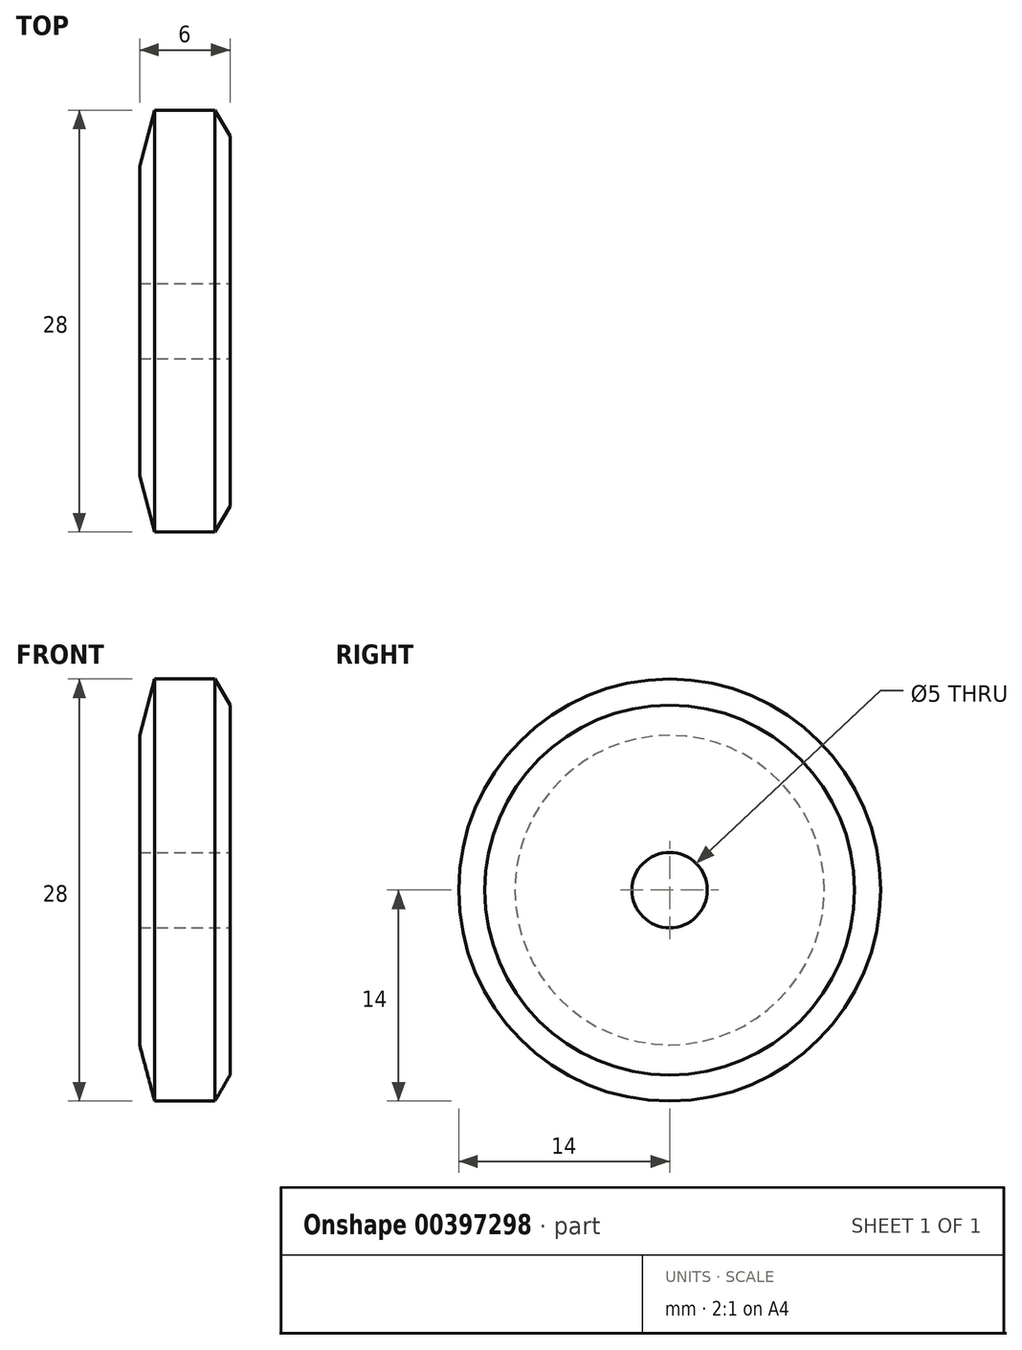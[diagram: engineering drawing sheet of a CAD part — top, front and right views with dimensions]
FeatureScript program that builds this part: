
annotation { "Feature Type Name" : "Feature", "Feature Type Description" : "" }
export const myFeature = defineFeature(function(context is Context, id is Id, definition is map)
    precondition{}
    {
        {
            var Q0;
            Q0=qCreatedBy(makeId("Front.planeOp"),FACE);
            var sketch = newSketch(context, id + "F0", { "sketchPlane" : qUnion([Q0])});
            skLineSegment(sketch, "E0", {"start": v(0, 0) * mm, "end": v(0, 14) * mm});
            skLineSegment(sketch, "E1", {"start": v(0, 14) * mm, "end": v(6, 14) * mm});
            skLineSegment(sketch, "E2", {"start": v(6, 14) * mm, "end": v(6, 0) * mm});
            skLineSegment(sketch, "E3", {"start": v(6, 0) * mm, "end": v(0, 0) * mm});
            skLineSegment(sketch, "E4", {"start": v(0, 3) * mm, "end": v(6, 3) * mm, "construction": true});
            skLineSegment(sketch, "E5", {"start": v(1, 14) * mm, "end": v(0, 10.27) * mm});
            skLineSegment(sketch, "E6", {"start": v(5, 14) * mm, "end": v(6, 12.27) * mm});
            skSolve(sketch);
        }
        {
            var Q0;
            {var subQ0=sQuery(id+"F0.wireOp",EDGE,"E3");Q0=makeQuery(id+"F0.imprint","IMPRINT",FACE,{"disambiguationData":[TD([[makeQuery(id+"F0.imprint","IMPRINT",EDGE,{"derivedFrom":subQ0}),-1.0]])]});}
            var Q1;
            Q1=sQuery(id+"F0.wireOp",EDGE,"E3");
            revolve(context, id + "F1", {"entities" : qUnion([Q0]), "axis" : qUnion([Q1]), "revolveType" : RevolveType.FULL});
        }
        {
            var Q0;
            Q0=makeQuery(id+"F1.opRevolve","SWEPT_FACE",FACE,{"disambiguationData":[OSD([sQuery(id+"F0.wireOp",EDGE,"E2")])]});
            var sketch = newSketch(context, id + "F2", { "sketchPlane" : qUnion([Q0])});
            skPoint(sketch, "E7", {"position": v(0, 0) * mm});
            skSolve(sketch);
        }
        {
            var Q0;
            Q0=sQuery(id+"F2.wireOp",VERTEX,"E7");
            var Q1;
            Q1=makeQuery(id+"F1.opRevolve","SWEPT_BODY",BODY,{"disambiguationData":[OSD([sQuery(id+"F0.wireOp",EDGE,"E0"),sQuery(id+"F0.wireOp",EDGE,"E1"),sQuery(id+"F0.wireOp",EDGE,"E2"),sQuery(id+"F0.wireOp",EDGE,"E3"),sQuery(id+"F0.wireOp",EDGE,"E5"),sQuery(id+"F0.wireOp",EDGE,"E6")])]});
            hole(context, id + "F3", {"style" : HoleStyle.SIMPLE, "endStyle" : HoleEndStyle.THROUGH, "standardTappedOrClearance" : lookupTablePath({ "standard" : "ISO", "engagement" : "75%", "pitch" : "1 mm", "size" : "M6", "type" : "Tapped" }), "standardBlindInLast" : lookupTablePath({ "standard" : "ISO", "engagement" : "75%", "pitch" : "1 mm", "size" : "M6", "type" : "Tapped" }), "holeDiameter" : 5 * mm, "showTappedDepth" : true, "isTappedThrough" : true, "tappedDepth" : 12 * mm, "tapClearance" : 3, "locations" : qUnion([Q0]), "scope" : qUnion([Q1]), "majorDiameter" : 6 * mm});
        }
    });
